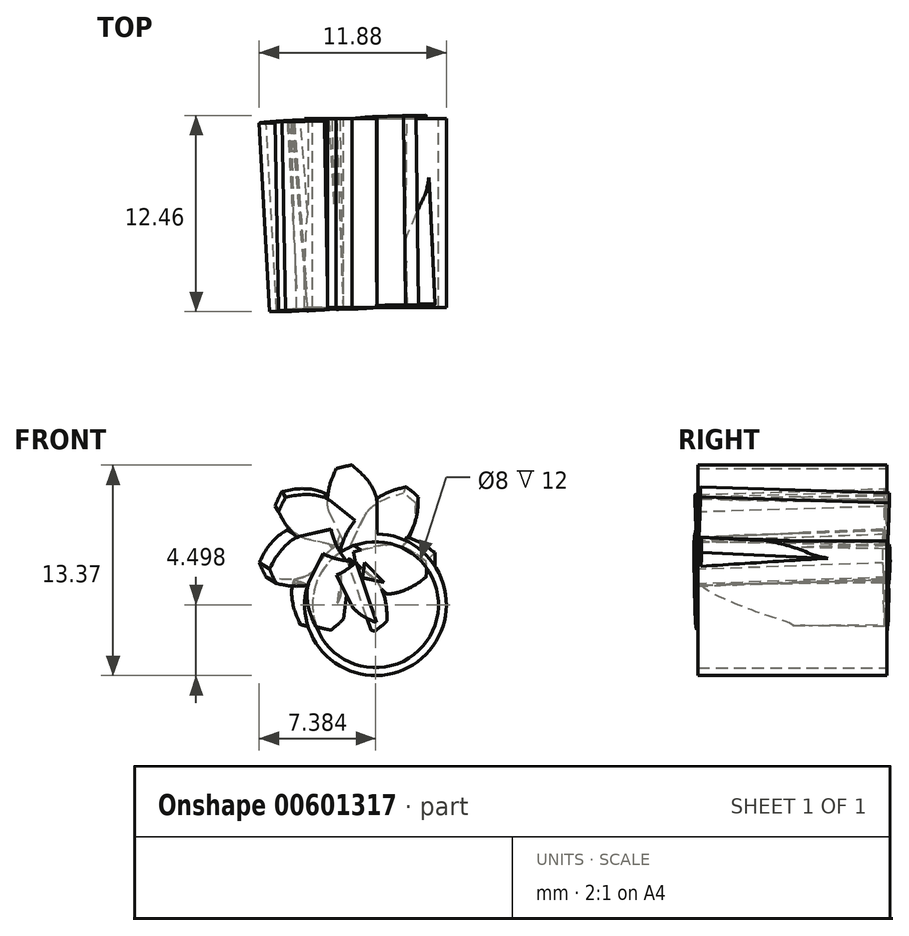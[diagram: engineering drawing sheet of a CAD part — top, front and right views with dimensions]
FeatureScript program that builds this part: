
annotation { "Feature Type Name" : "Feature", "Feature Type Description" : "" }
export const myFeature = defineFeature(function(context is Context, id is Id, definition is map)
    precondition{}
    {
        {
            assignVariable(context, id + "F0", {"name" : "module", "anyValue" : 2});
        }
        {
            assignVariable(context, id + "F1", {"name" : "pitchDiameter", "anyValue" : 14});
        }
        {
            assignVariable(context, id + "F2", {"name" : "numberOfTeeth", "anyValue" : getVariable(context, 'pitchDiameter') / getVariable(context, 'module')});
        }
        {
            assignVariable(context, id + "F3", {"name" : "thickness", "anyValue" : 12});
        }
        {
            var Q0;
            Q0=qCreatedBy(makeId("Front.planeOp"),FACE);
            var sketch = newSketch(context, id + "F4", { "sketchPlane" : qUnion([Q0])});
            skCircle(sketch, "E0", {"center": v(-37.02, 49.5) * mm, "radius": 7 * mm, "construction": true});
            skLineSegment(sketch, "E1", {"start": v(-37.02, 49.5) * mm, "end": v(-37.02, 66.5) * mm, "construction": true});
            skPoint(sketch, "E2", {"position": v(-37.02, 56.5) * mm});
            skLineSegment(sketch, "E3", {"start": v(-66.46, 56.5) * mm, "end": v(-7.57, 56.5) * mm, "construction": true});
            skLineSegment(sketch, "E4", {"start": v(-61.63, 47.55) * mm, "end": v(-12.4, 65.47) * mm, "construction": true});
            skLineSegment(sketch, "E5", {"start": v(-37.02, 49.5) * mm, "end": v(-39.27, 55.69) * mm, "construction": true});
            skCircle(sketch, "E6", {"center": v(-37.02, 49.5) * mm, "radius": 6.58 * mm, "construction": true});
            skArc(sketch, "E7", {"start": v(-39.27, 55.69) * mm, "mid": v(-40.91, 54.8) * mm, "end": v(-42.25, 53.5) * mm, "construction": true});
            skLineSegment(sketch, "E8", {"start": v(-42.25, 53.5) * mm, "end": v(-37.02, 49.5) * mm, "construction": true});
            skLineSegment(sketch, "E9", {"start": v(-42.25, 53.5) * mm, "end": v(-38.52, 58.38) * mm, "construction": true});
            skArc(sketch, "E10", {"start": v(-39.27, 55.69) * mm, "mid": v(-38.65, 55.88) * mm, "end": v(-38.02, 56) * mm, "construction": true});
            skLineSegment(sketch, "E11", {"start": v(-38.02, 56) * mm, "end": v(-37.02, 49.5) * mm, "construction": true});
            skLineSegment(sketch, "E12", {"start": v(-38.02, 56) * mm, "end": v(-36.93, 56.18) * mm, "construction": true});
            skArc(sketch, "E13", {"start": v(-36.92, 56.09) * mm, "mid": v(-38.11, 56) * mm, "end": v(-39.27, 55.69) * mm, "construction": true});
            skArc(sketch, "E14", {"start": v(-38.76, 55.85) * mm, "mid": v(-39.01, 55.78) * mm, "end": v(-39.27, 55.69) * mm, "construction": true});
            skLineSegment(sketch, "E15", {"start": v(-38.76, 55.85) * mm, "end": v(-37.02, 49.5) * mm, "construction": true});
            skLineSegment(sketch, "E16", {"start": v(-38.76, 55.85) * mm, "end": v(-36.96, 56.34) * mm, "construction": true});
            skArc(sketch, "E17", {"start": v(-39.27, 55.69) * mm, "mid": v(-39.14, 55.73) * mm, "end": v(-39.02, 55.77) * mm});
            skLineSegment(sketch, "E18", {"start": v(-39.02, 55.77) * mm, "end": v(-37.02, 49.5) * mm, "construction": true});
            skLineSegment(sketch, "E19", {"start": v(-39.02, 55.77) * mm, "end": v(-36.99, 56.42) * mm, "construction": true});
            skArc(sketch, "E20", {"start": v(-39.27, 55.69) * mm, "mid": v(-38.86, 55.82) * mm, "end": v(-38.44, 55.93) * mm});
            skLineSegment(sketch, "E21", {"start": v(-38.44, 55.93) * mm, "end": v(-37.02, 49.5) * mm, "construction": true});
            skLineSegment(sketch, "E22", {"start": v(-38.44, 55.93) * mm, "end": v(-36.94, 56.26) * mm, "construction": true});
            skArc(sketch, "E23", {"start": v(-39.27, 55.69) * mm, "mid": v(-40.53, 55.07) * mm, "end": v(-41.63, 54.2) * mm});
            skLineSegment(sketch, "E24", {"start": v(-41.63, 54.2) * mm, "end": v(-37.02, 49.5) * mm, "construction": true});
            skLineSegment(sketch, "E25", {"start": v(-41.63, 54.2) * mm, "end": v(-37.91, 57.85) * mm, "construction": true});
            skArc(sketch, "E26", {"start": v(-39.27, 55.69) * mm, "mid": v(-40.12, 55.3) * mm, "end": v(-40.91, 54.8) * mm});
            skLineSegment(sketch, "E27", {"start": v(-40.91, 54.8) * mm, "end": v(-37.02, 49.5) * mm, "construction": true});
            skLineSegment(sketch, "E28", {"start": v(-40.91, 54.8) * mm, "end": v(-37.47, 57.34) * mm, "construction": true});
            skArc(sketch, "E29", {"start": v(-39.27, 55.69) * mm, "mid": v(-39.7, 55.51) * mm, "end": v(-40.12, 55.3) * mm});
            skLineSegment(sketch, "E30", {"start": v(-40.12, 55.3) * mm, "end": v(-37.02, 49.5) * mm, "construction": true});
            skLineSegment(sketch, "E31", {"start": v(-40.12, 55.3) * mm, "end": v(-37.18, 56.88) * mm, "construction": true});
            skLineSegment(sketch, "E32", {"start": v(-38.52, 58.38) * mm, "end": v(-37.02, 49.5) * mm, "construction": true});
            skSolve(sketch);
        }
        {
            var Q0;
            Q0=qCreatedBy(makeId("Front.planeOp"),FACE);
            var sketch = newSketch(context, id + "F5", { "sketchPlane" : qUnion([Q0])});
            skPoint(sketch, "E33", {"position": v(-37.02, 56.5) * mm});
            skPoint(sketch, "E34", {"position": v(-37.02, 49.5) * mm});
            skLineSegment(sketch, "E35", {"start": v(-37.02, 49.5) * mm, "end": v(-40.13, 63.16) * mm, "construction": true});
            skCircle(sketch, "E36", {"center": v(-37.02, 49.5) * mm, "radius": 6.58 * mm, "construction": true});
            skPoint(sketch, "E37", {"position": v(-37.02, 63.5) * mm});
            skLineSegment(sketch, "E38", {"start": v(-37.02, 63.5) * mm, "end": v(-37.02, 49.5) * mm, "construction": true});
            skCircle(sketch, "E39", {"center": v(-37.02, 49.5) * mm, "radius": 4.5 * mm, "construction": true});
            skPoint(sketch, "E40.0", {"position": v(-37.47, 57.34) * mm});
            skPoint(sketch, "E41.0", {"position": v(-37.18, 56.88) * mm});
            skPoint(sketch, "E42.0", {"position": v(-37.91, 57.85) * mm});
            skPoint(sketch, "E43.0", {"position": v(-36.99, 56.42) * mm});
            skPoint(sketch, "E44.0", {"position": v(-36.96, 56.34) * mm});
            skPoint(sketch, "E45.0", {"position": v(-36.94, 56.26) * mm});
            skPoint(sketch, "E46.0", {"position": v(-36.93, 56.18) * mm});
            skPoint(sketch, "E47.0", {"position": v(-36.92, 56.09) * mm});
            skPoint(sketch, "E48.0", {"position": v(-38.52, 58.38) * mm});
            skFitSpline(sketch, "E49", {"points": [v(-36.92, 56.09) * mm, v(-36.93, 56.18) * mm, v(-36.94, 56.26) * mm, v(-36.96, 56.34) * mm, v(-36.99, 56.42) * mm, v(-37.02, 56.5) * mm, v(-37.18, 56.88) * mm, v(-37.47, 57.34) * mm, v(-37.91, 57.85) * mm, v(-38.52, 58.38) * mm], "startDerivative": vector(-3.67, 6.97) * mm, "endDerivative": vector(-4.38, 4.04) * mm});
            skArc(sketch, "E50", {"start": v(-38.52, 58.38) * mm, "mid": v(-38.77, 58.34) * mm, "end": v(-39.02, 58.28) * mm});
            skFitSpline(sketch, "E51.MirrorCS", {"points": [v(-39.96, 55.4) * mm, v(-39.99, 55.48) * mm, v(-40.01, 55.56) * mm, v(-40.03, 55.64) * mm, v(-40.04, 55.73) * mm, v(-40.05, 55.81) * mm, v(-40.06, 56.22) * mm, v(-40, 56.76) * mm, v(-39.83, 57.41) * mm, v(-39.51, 58.15) * mm], "startDerivative": vector(0.28, 7.87) * mm, "endDerivative": vector(2.2, 5.54) * mm});
            skArc(sketch, "E52.MirrorCS", {"start": v(-39.51, 58.15) * mm, "mid": v(-39.27, 58.22) * mm, "end": v(-39.02, 58.28) * mm});
            skLineSegment(sketch, "E53", {"start": v(-36.92, 56.09) * mm, "end": v(-36.92, 54) * mm});
            skArc(sketch, "E54", {"start": v(-36.92, 54) * mm, "mid": v(-37.47, 53.99) * mm, "end": v(-38.02, 53.9) * mm});
            skLineSegment(sketch, "E55.MirrorCS", {"start": v(-39.96, 55.4) * mm, "end": v(-39.06, 53.52) * mm});
            skArc(sketch, "E56.MirrorCS", {"start": v(-39.06, 53.52) * mm, "mid": v(-38.55, 53.74) * mm, "end": v(-38.02, 53.9) * mm});
            skSolve(sketch);
        }
        {
            var Q0;
            Q0=qCreatedBy(makeId("Front.planeOp"),FACE);
            var sketch = newSketch(context, id + "F6", { "sketchPlane" : qUnion([Q0])});
            skCircle(sketch, "E57.0", {"center": v(-37.02, 49.5) * mm, "radius": 4.5 * mm});
            skFitSpline(sketch, "E58.1.0", {"points": [v(-39.44, 58.37) * mm, v(-39.55, 58.09) * mm, v(-39.7, 57.8) * mm, v(-39.9, 57.19) * mm, v(-40.05, 56.7) * mm, v(-40.15, 56.26) * mm, v(-40.18, 56.02) * mm, v(-40.21, 55.78) * mm, v(-40.23, 55.57) * mm, v(-40.25, 55.25) * mm, v(-40.2, 55.32) * mm, v(-40.22, 55.07) * mm]});
            skLineSegment(sketch, "E58.1.1", {"start": v(-39.96, 55.4) * mm, "end": v(-39.06, 53.52) * mm});
            skArc(sketch, "E58.1.2", {"start": v(-39.06, 53.52) * mm, "mid": v(-38.55, 53.74) * mm, "end": v(-38.02, 53.9) * mm});
            skArc(sketch, "E58.1.3", {"start": v(-38.02, 53.9) * mm, "mid": v(-37.47, 53.99) * mm, "end": v(-36.92, 54) * mm});
            skLineSegment(sketch, "E58.1.4", {"start": v(-36.92, 54) * mm, "end": v(-36.92, 56.09) * mm});
            skFitSpline(sketch, "E58.1.5", {"points": [v(-36.75, 55.36) * mm, v(-36.8, 55.6) * mm, v(-36.75, 55.54) * mm, v(-36.82, 55.86) * mm, v(-36.87, 56.06) * mm, v(-36.94, 56.29) * mm, v(-37.02, 56.51) * mm, v(-37.19, 56.94) * mm, v(-37.4, 57.4) * mm, v(-37.7, 57.96) * mm, v(-37.9, 58.22) * mm, v(-38.06, 58.48) * mm]});
            skArc(sketch, "E58.1.6", {"start": v(-38.52, 58.38) * mm, "mid": v(-38.77, 58.34) * mm, "end": v(-39.02, 58.28) * mm});
            skArc(sketch, "E58.1.7", {"start": v(-39.02, 58.28) * mm, "mid": v(-39.27, 58.22) * mm, "end": v(-39.51, 58.15) * mm});
            skSolve(sketch);
        }
        {
            var Q0;
            {var subQ0=sQuery(id+"F6.wireOp",EDGE,"E57.0");var subQ1=makeQuery(id+"F6.imprint","INTERSECT",VERTEX,{"derivedFrom":[subQ0,sQuery(id+"F6.wireOp",EDGE,"E58.1.1")]});Q0=makeQuery(id+"F6.imprint","IMPRINT",FACE,{"disambiguationData":[TD([[makeQuery(id+"F6.imprint","IMPRINT",EDGE,{"disambiguationData":[TD([[subQ1,1.0]])],"derivedFrom":subQ0}),1.0]])]});}
            var Q1;
            Q1=makeQuery(id+"F6.imprint","IMPRINT",FACE,{"disambiguationData":[TD([[makeQuery(id+"F6.imprint","IMPRINT",EDGE,{"derivedFrom":sQuery(id+"F6.wireOp",EDGE,"E58.1.0")}),1.0]])]});
            extrude(context, id + "F7", {"entities" : qUnion([Q0, Q1]), "depth" : (getVariable(context, 'thickness')) * mm, "offsetDistance" : 25 * mm});
        }
        {
            var Q0;
            Q0=makeQuery(id+"F5.imprint","IMPRINT",FACE,{"disambiguationData":[TD([[makeQuery(id+"F5.imprint","IMPRINT",EDGE,{"derivedFrom":sQuery(id+"F5.wireOp",EDGE,"E49")}),1.0]])]});
            extrude(context, id + "F8", {"entities" : qUnion([Q0]), "depth" : (getVariable(context, 'thickness')) * mm, "offsetDistance" : 25 * mm});
        }
        {
            var Q0;
            Q0=makeQuery(id+"F8.opExtrude","CAP_EDGE",EDGE,{"disambiguationData":[OSD([sQuery(id+"F5.wireOp",EDGE,"E50"),sQuery(id+"F5.wireOp",EDGE,"E52.MirrorCS")])],"isStart":false});
            cPoint(context, id + "F9", {"entities" : qUnion([Q0]), "parameter" : 0.5});
        }
        {
            var Q0;
            Q0=qCreatedBy(id+"F9",VERTEX);
            var Q1;
            Q1=sQuery(id+"F5.wireOp",VERTEX,"E52.MirrorCS.end");
            var Q2;
            Q2=sQuery(id+"F5.wireOp",VERTEX,"E56.MirrorCS.end");
            cPlane(context, id + "F10", {"entities" : qUnion([Q0, Q1, Q2]), "cplaneType" : CPlaneType.THREE_POINT, "offset" : 0 * mm, "width" : 150 * mm, "height" : 150 * mm});
        }
        {
            var Q0;
            Q0=qCreatedBy(id+"F10.planeOp",FACE);
            var sketch = newSketch(context, id + "F11", { "sketchPlane" : qUnion([Q0])});
            skPoint(sketch, "E59.0", {"position": v(0, 56.5) * mm});
            skLineSegment(sketch, "E60", {"start": v(0, 56.5) * mm, "end": v(30.78, 56.5) * mm, "construction": true});
            skSolve(sketch);
        }
        {
            var Q0;
            Q0=makeQuery(id+"F8.opExtrude","SWEPT_BODY",BODY,{"disambiguationData":[OSD([sQuery(id+"F5.wireOp",EDGE,"E49"),sQuery(id+"F5.wireOp",EDGE,"E50"),sQuery(id+"F5.wireOp",EDGE,"E51.MirrorCS"),sQuery(id+"F5.wireOp",EDGE,"E52.MirrorCS"),sQuery(id+"F5.wireOp",EDGE,"E53"),sQuery(id+"F5.wireOp",EDGE,"E54"),sQuery(id+"F5.wireOp",EDGE,"E55.MirrorCS"),sQuery(id+"F5.wireOp",EDGE,"E56.MirrorCS")])]});
            var Q1;
            Q1=sQuery(id+"F11.wireOp",EDGE,"E60");
            circularPattern(context, id + "F12", {"operationType" : NewBodyOperationType.ADD, "entities" : qUnion([Q0]), "axis" : qUnion([Q1]), "angle" : 360 * degree, "instanceCount" : getVariable(context, 'numberOfTeeth'), "equalSpace" : true});
        }
        {
            var Q0;
            Q0=qCreatedBy(makeId("Front.planeOp"),FACE);
            var sketch = newSketch(context, id + "F13", { "sketchPlane" : qUnion([Q0])});
            skPoint(sketch, "E61.0", {"position": v(-37.02, 49.5) * mm});
            skCircle(sketch, "E62", {"center": v(-37.02, 49.5) * mm, "radius": 4 * mm});
            skSolve(sketch);
        }
        {
            var Q0;
            Q0=makeQuery(id+"F13.imprint","IMPRINT",FACE,{"disambiguationData":[TD([[makeQuery(id+"F13.imprint","IMPRINT",EDGE,{"derivedFrom":sQuery(id+"F13.wireOp",EDGE,"E62")}),1.0]])]});
            extrude(context, id + "F14", {"entities" : qUnion([Q0]), "operationType" : NewBodyOperationType.REMOVE, "depth" : (getVariable(context, 'thickness')) * mm, "offsetDistance" : 25 * mm});
        }
    });
